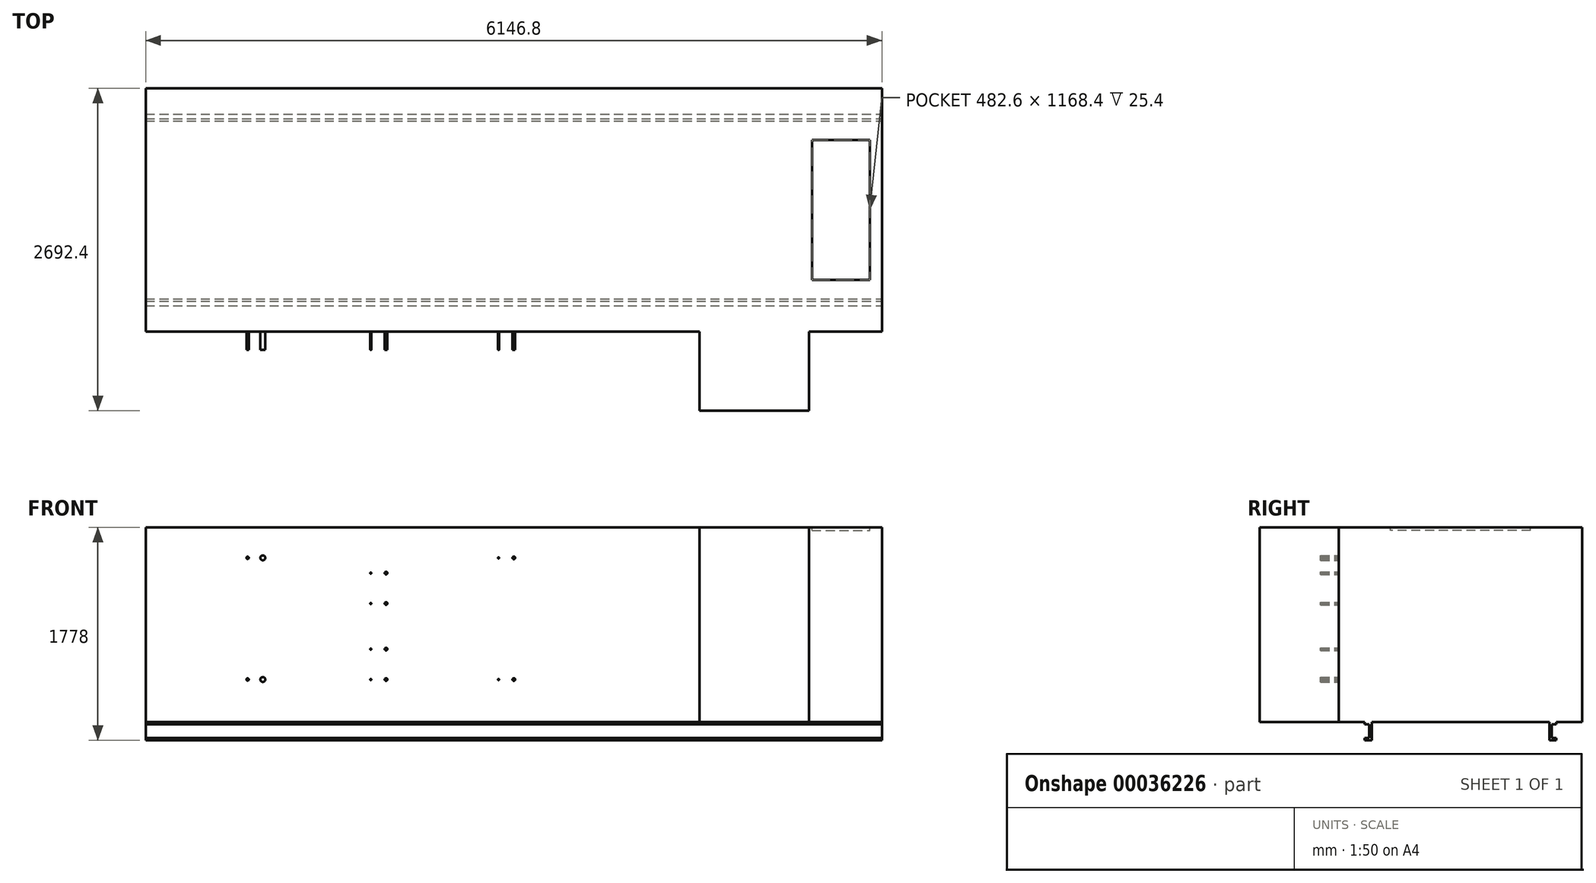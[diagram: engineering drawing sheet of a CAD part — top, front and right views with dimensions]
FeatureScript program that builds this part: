
annotation { "Feature Type Name" : "Feature", "Feature Type Description" : "" }
export const myFeature = defineFeature(function(context is Context, id is Id, definition is map)
    precondition{}
    {
        {
            var Q0;
            Q0=qCreatedBy(makeId("Front.planeOp"),FACE);
            var sketch = newSketch(context, id + "F0", { "sketchPlane" : qUnion([Q0])});
            skLineSegment(sketch, "E0.bottom", {"start": v(0, 0) * mm, "end": v(6146.8, 0) * mm});
            skLineSegment(sketch, "E0.top", {"start": v(0, 1625.6) * mm, "end": v(6146.8, 1625.6) * mm});
            skLineSegment(sketch, "E0.left", {"start": v(0, 0) * mm, "end": v(0, 1625.6) * mm});
            skLineSegment(sketch, "E0.right", {"start": v(6146.8, 0) * mm, "end": v(6146.8, 1625.6) * mm});
            skSolve(sketch);
        }
        {
            var Q0;
            Q0 = qSketchRegion(id + "F0", true);
            extrude(context, id + "F1", {"entities" : qUnion([Q0]), "depth" : 2032 * mm});
        }
        {
            var Q0;
            Q0=makeQuery(id+"F1.opExtrude","CAP_FACE",FACE,{"disambiguationData":[OSD([sQuery(id+"F0.wireOp",EDGE,"E0.bottom"),sQuery(id+"F0.wireOp",EDGE,"E0.top"),sQuery(id+"F0.wireOp",EDGE,"E0.left"),sQuery(id+"F0.wireOp",EDGE,"E0.right")])],"isStart":false});
            var sketch = newSketch(context, id + "F2", { "sketchPlane" : qUnion([Q0])});
            skLineSegment(sketch, "E1.bottom", {"start": v(4622.8, 0) * mm, "end": v(5537.2, 0) * mm});
            skLineSegment(sketch, "E1.top", {"start": v(4622.8, 1625.6) * mm, "end": v(5537.2, 1625.6) * mm});
            skLineSegment(sketch, "E1.left", {"start": v(4622.8, 0) * mm, "end": v(4622.8, 1625.6) * mm});
            skLineSegment(sketch, "E1.right", {"start": v(5537.2, 0) * mm, "end": v(5537.2, 1625.6) * mm});
            skSolve(sketch);
        }
        {
            var Q0;
            Q0 = qSketchRegion(id + "F2", true);
            extrude(context, id + "F3", {"entities" : qUnion([Q0]), "operationType" : NewBodyOperationType.ADD, "depth" : 660.4 * mm});
        }
        {
            var Q0;
            Q0=makeQuery(id+"F3.boolean.opBoolean","MERGE",FACE,{"derivedFrom":[makeQuery(id+"F1.opExtrude","SWEPT_FACE",FACE,{"disambiguationData":[OSD([sQuery(id+"F0.wireOp",EDGE,"E0.top")])]}),makeQuery(id+"F3.opExtrude","SWEPT_FACE",FACE,{"disambiguationData":[OSD([sQuery(id+"F2.wireOp",EDGE,"E1.top")])]})]});
            var sketch = newSketch(context, id + "F4", { "sketchPlane" : qUnion([Q0])});
            skLineSegment(sketch, "E2.bottom", {"start": v(5562.6, -431.8) * mm, "end": v(6045.2, -431.8) * mm});
            skLineSegment(sketch, "E2.top", {"start": v(5562.6, -1600.2) * mm, "end": v(6045.2, -1600.2) * mm});
            skLineSegment(sketch, "E2.left", {"start": v(5562.6, -431.8) * mm, "end": v(5562.6, -1600.2) * mm});
            skLineSegment(sketch, "E2.right", {"start": v(6045.2, -431.8) * mm, "end": v(6045.2, -1600.2) * mm});
            skSolve(sketch);
        }
        {
            var Q0;
            Q0 = qSketchRegion(id + "F4", true);
            extrude(context, id + "F5", {"entities" : qUnion([Q0]), "operationType" : NewBodyOperationType.REMOVE, "oppositeDirection" : true, "depth" : 25.4 * mm});
        }
        {
            var Q0;
            Q0=makeQuery(id+"F1.opExtrude","SWEPT_FACE",FACE,{"disambiguationData":[OSD([sQuery(id+"F0.wireOp",EDGE,"E0.right")])]});
            var sketch = newSketch(context, id + "F6", { "sketchPlane" : qUnion([Q0])});
            skLineSegment(sketch, "E3", {"start": v(-1816.1, 0) * mm, "end": v(-1816.1, -20.32) * mm});
            skLineSegment(sketch, "E4", {"start": v(-1816.1, -20.32) * mm, "end": v(-1778, -20.32) * mm});
            skLineSegment(sketch, "E5", {"start": v(-1778, -20.32) * mm, "end": v(-1778, -132.08) * mm});
            skLineSegment(sketch, "E6", {"start": v(-1778, -132.08) * mm, "end": v(-1816.1, -132.08) * mm});
            skLineSegment(sketch, "E7", {"start": v(-1816.1, -132.08) * mm, "end": v(-1816.1, -152.4) * mm});
            skLineSegment(sketch, "E8", {"start": v(-1816.1, -152.4) * mm, "end": v(-1757.68, -152.4) * mm});
            skLineSegment(sketch, "E9", {"start": v(-1757.68, -152.4) * mm, "end": v(-1757.68, 0) * mm});
            skLineSegment(sketch, "E10", {"start": v(-1757.68, 0) * mm, "end": v(-1816.1, 0) * mm});
            skLineSegment(sketch, "E11", {"start": v(-1016, 0) * mm, "end": v(-1016, 625.35) * mm, "construction": true});
            skLineSegment(sketch, "E12.MirrorCS", {"start": v(-215.9, -132.08) * mm, "end": v(-215.9, -152.4) * mm});
            skLineSegment(sketch, "E13.MirrorCS", {"start": v(-274.32, 0) * mm, "end": v(-215.9, 0) * mm});
            skLineSegment(sketch, "E14.MirrorCS", {"start": v(-274.32, -152.4) * mm, "end": v(-274.32, 0) * mm});
            skLineSegment(sketch, "E15.MirrorCS", {"start": v(-215.9, -152.4) * mm, "end": v(-274.32, -152.4) * mm});
            skLineSegment(sketch, "E16.MirrorCS", {"start": v(-254, -132.08) * mm, "end": v(-215.9, -132.08) * mm});
            skLineSegment(sketch, "E17.MirrorCS", {"start": v(-254, -20.32) * mm, "end": v(-254, -132.08) * mm});
            skLineSegment(sketch, "E18.MirrorCS", {"start": v(-215.9, -20.32) * mm, "end": v(-254, -20.32) * mm});
            skLineSegment(sketch, "E19.MirrorCS", {"start": v(-215.9, 0) * mm, "end": v(-215.9, -20.32) * mm});
            skSolve(sketch);
        }
        {
            var Q0;
            Q0 = qSketchRegion(id + "F6", true);
            var Q1;
            Q1=makeQuery(id+"F1.opExtrude","SWEPT_FACE",FACE,{"disambiguationData":[OSD([sQuery(id+"F0.wireOp",EDGE,"E0.left")])]});
            extrude(context, id + "F7", {"entities" : qUnion([Q0]), "operationType" : NewBodyOperationType.ADD, "endBound" : BoundingType.UP_TO_SURFACE, "oppositeDirection" : true, "endBoundEntityFace" : qUnion([Q1]), "depth" : 25.4 * mm});
        }
        {
            var Q0;
            {var subQ1=sQuery(id+"F2.wireOp",EDGE,"E1.left");Q0=makeQuery(id+"F2.imprint","IMPRINT",FACE,{"disambiguationData":[TD([[makeQuery(id+"F2.imprint","IMPRINT",EDGE,{"derivedFrom":subQ1}),1.0]])]});}
            var sketch = newSketch(context, id + "F8", { "sketchPlane" : qUnion([Q0])});
            skCircle(sketch, "E20", {"center": v(850.9, 1371.6) * mm, "radius": 9.53 * mm});
            skCircle(sketch, "E21", {"center": v(850.9, 355.6) * mm, "radius": 9.53 * mm});
            skCircle(sketch, "E22", {"center": v(977.9, 1371.6) * mm, "radius": 20.64 * mm});
            skCircle(sketch, "E23", {"center": v(977.9, 355.6) * mm, "radius": 20.64 * mm});
            skCircle(sketch, "E24", {"center": v(2946.4, 1371.6) * mm, "radius": 4.76 * mm});
            skCircle(sketch, "E25", {"center": v(3073.4, 1371.6) * mm, "radius": 11.11 * mm});
            skCircle(sketch, "E26", {"center": v(2946.4, 355.6) * mm, "radius": 4.76 * mm});
            skCircle(sketch, "E27", {"center": v(3073.4, 355.6) * mm, "radius": 11.11 * mm});
            skCircle(sketch, "E28", {"center": v(1879.6, 1244.6) * mm, "radius": 4.76 * mm});
            skCircle(sketch, "E29", {"center": v(2006.6, 1244.6) * mm, "radius": 11.11 * mm});
            skCircle(sketch, "E30", {"center": v(1879.6, 990.6) * mm, "radius": 4.76 * mm});
            skCircle(sketch, "E31", {"center": v(2006.6, 990.6) * mm, "radius": 11.11 * mm});
            skCircle(sketch, "E32", {"center": v(1879.6, 609.6) * mm, "radius": 4.76 * mm});
            skCircle(sketch, "E33", {"center": v(2006.6, 609.6) * mm, "radius": 11.11 * mm});
            skCircle(sketch, "E34", {"center": v(1879.6, 355.6) * mm, "radius": 4.76 * mm});
            skCircle(sketch, "E35", {"center": v(2006.6, 355.6) * mm, "radius": 11.11 * mm});
            skLineSegment(sketch, "E36.bottom", {"start": v(2946.4, 1371.6) * mm, "end": v(3073.4, 1371.6) * mm, "construction": true});
            skLineSegment(sketch, "E36.top", {"start": v(2946.4, 355.6) * mm, "end": v(3073.4, 355.6) * mm, "construction": true});
            skLineSegment(sketch, "E36.left", {"start": v(2946.4, 1371.6) * mm, "end": v(2946.4, 355.6) * mm, "construction": true});
            skLineSegment(sketch, "E36.right", {"start": v(3073.4, 1371.6) * mm, "end": v(3073.4, 355.6) * mm, "construction": true});
            skLineSegment(sketch, "E37.bottom", {"start": v(1879.6, 1244.6) * mm, "end": v(2006.6, 1244.6) * mm, "construction": true});
            skLineSegment(sketch, "E37.top", {"start": v(1879.6, 990.6) * mm, "end": v(2006.6, 990.6) * mm, "construction": true});
            skLineSegment(sketch, "E37.left", {"start": v(1879.6, 1244.6) * mm, "end": v(1879.6, 990.6) * mm, "construction": true});
            skLineSegment(sketch, "E37.right", {"start": v(2006.6, 1244.6) * mm, "end": v(2006.6, 990.6) * mm, "construction": true});
            skLineSegment(sketch, "E38.bottom", {"start": v(1879.6, 609.6) * mm, "end": v(2006.6, 609.6) * mm, "construction": true});
            skLineSegment(sketch, "E38.top", {"start": v(1879.6, 355.6) * mm, "end": v(2006.6, 355.6) * mm, "construction": true});
            skLineSegment(sketch, "E38.left", {"start": v(1879.6, 609.6) * mm, "end": v(1879.6, 355.6) * mm, "construction": true});
            skLineSegment(sketch, "E38.right", {"start": v(2006.6, 609.6) * mm, "end": v(2006.6, 355.6) * mm, "construction": true});
            skLineSegment(sketch, "E39.bottom", {"start": v(850.9, 1371.6) * mm, "end": v(977.9, 1371.6) * mm, "construction": true});
            skLineSegment(sketch, "E39.top", {"start": v(850.9, 355.6) * mm, "end": v(977.9, 355.6) * mm, "construction": true});
            skLineSegment(sketch, "E39.left", {"start": v(850.9, 1371.6) * mm, "end": v(850.9, 355.6) * mm, "construction": true});
            skLineSegment(sketch, "E39.right", {"start": v(977.9, 1371.6) * mm, "end": v(977.9, 355.6) * mm, "construction": true});
            skSolve(sketch);
        }
        {
            var Q0;
            Q0 = qSketchRegion(id + "F8", true);
            extrude(context, id + "F9", {"entities" : qUnion([Q0]), "operationType" : NewBodyOperationType.ADD, "depth" : 152.4 * mm});
        }
    });
